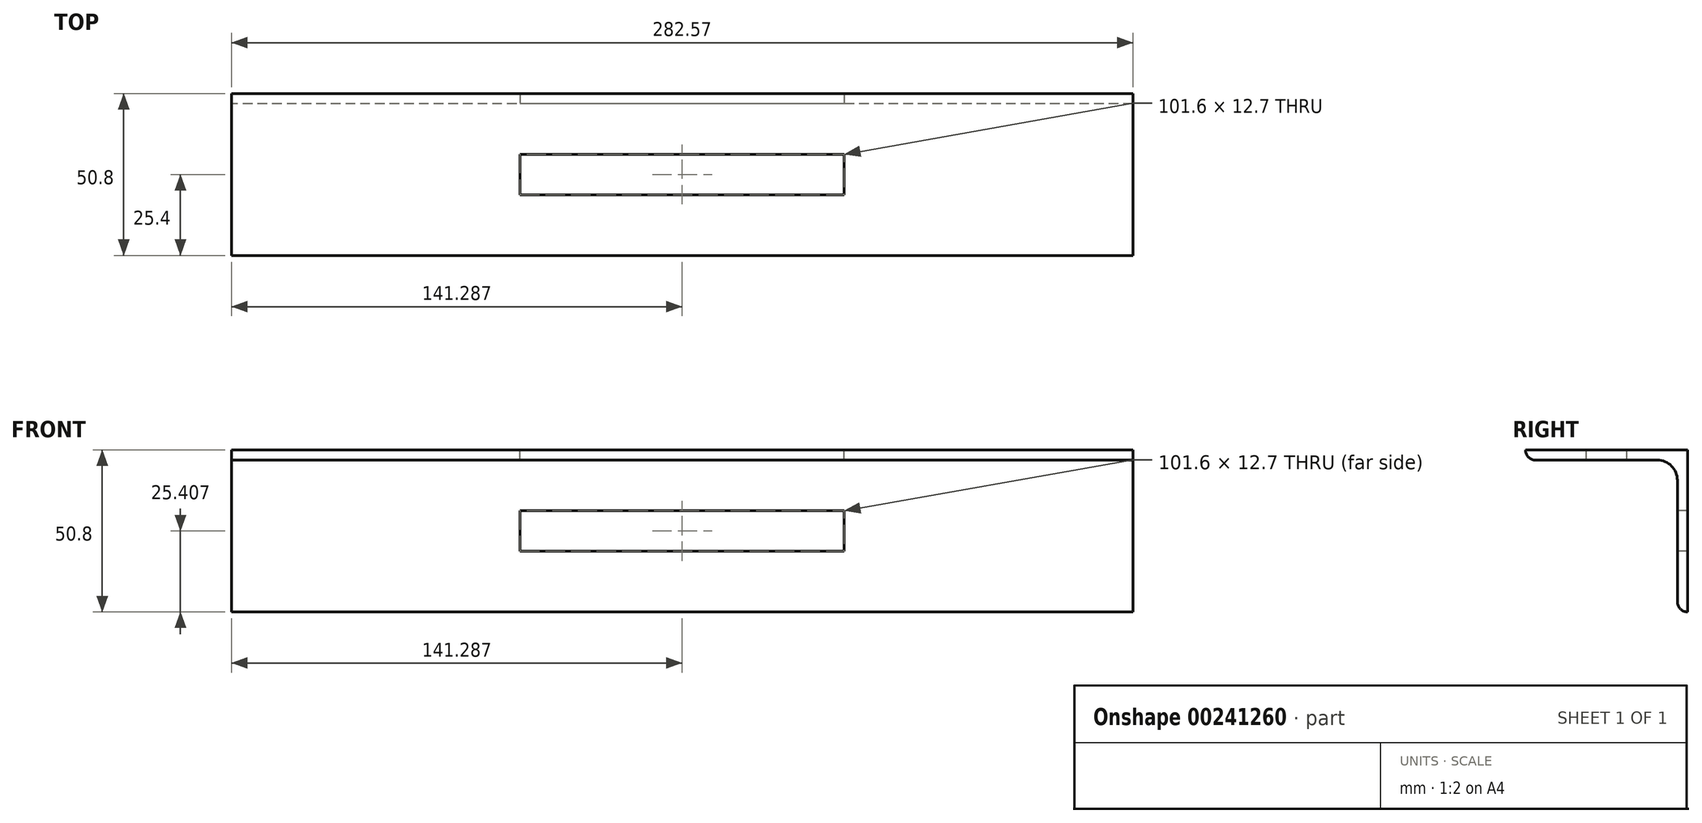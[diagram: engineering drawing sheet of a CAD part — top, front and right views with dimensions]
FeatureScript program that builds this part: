
annotation { "Feature Type Name" : "Feature", "Feature Type Description" : "" }
export const myFeature = defineFeature(function(context is Context, id is Id, definition is map)
    precondition{}
    {
        {
            var Q0;
            Q0=qCreatedBy(makeId("Right.planeOp"),FACE);
            var sketch = newSketch(context, id + "F0", { "sketchPlane" : qUnion([Q0])});
            skLineSegment(sketch, "E0", {"start": v(0, -7.2) * mm, "end": v(0, 43.6) * mm});
            skLineSegment(sketch, "E1", {"start": v(0, 43.6) * mm, "end": v(-50.8, 43.6) * mm});
            skLineSegment(sketch, "E2", {"start": v(-50.8, 43.6) * mm, "end": v(-50.8, 43.6) * mm});
            skLineSegment(sketch, "E3", {"start": v(-47.63, 40.43) * mm, "end": v(-9.52, 40.43) * mm});
            skLineSegment(sketch, "E4", {"start": v(-3.17, 34.08) * mm, "end": v(-3.17, -4.02) * mm});
            skLineSegment(sketch, "E5", {"start": v(-0.1, -7.19) * mm, "end": v(0, -7.2) * mm});
            skPoint(sketch, "E6.visualSharp", {"position": v(-3.17, -7.09) * mm});
            skArc(sketch, "E6.filletArc", {"start": v(-3.17, -4.02) * mm, "mid": v(-2.28, -6.22) * mm, "end": v(-0.1, -7.19) * mm});
            skPoint(sketch, "E7.visualSharp", {"position": v(-50.8, 40.43) * mm});
            skArc(sketch, "E7.filletArc", {"start": v(-50.8, 43.6) * mm, "mid": v(-49.87, 41.36) * mm, "end": v(-47.63, 40.43) * mm});
            skPoint(sketch, "E8.visualSharp", {"position": v(-3.17, 40.43) * mm});
            skArc(sketch, "E8.filletArc", {"start": v(-3.17, 34.08) * mm, "mid": v(-5.03, 38.57) * mm, "end": v(-9.52, 40.43) * mm});
            skSolve(sketch);
        }
        {
            var Q0;
            Q0=makeQuery(id+"F0.imprint","IMPRINT",FACE,{"disambiguationData":[TD([[makeQuery(id+"F0.imprint","IMPRINT",EDGE,{"derivedFrom":sQuery(id+"F0.wireOp",EDGE,"E0")}),1.0]])]});
            extrude(context, id + "F1", {"entities" : qUnion([Q0]), "depth" : 282.57 * mm});
        }
        {
            var Q0;
            Q0=makeQuery(id+"F1.opExtrude","SWEPT_BODY",BODY,{"disambiguationData":[OSD([sQuery(id+"F0.wireOp",EDGE,"E0"),sQuery(id+"F0.wireOp",EDGE,"E1"),sQuery(id+"F0.wireOp",EDGE,"E3"),sQuery(id+"F0.wireOp",EDGE,"E4"),sQuery(id+"F0.wireOp",EDGE,"E5"),sQuery(id+"F0.wireOp",EDGE,"E6.filletArc"),sQuery(id+"F0.wireOp",EDGE,"E7.filletArc"),sQuery(id+"F0.wireOp",EDGE,"E8.filletArc")])]});
            transform(context, id + "F2", {"entities" : qUnion([Q0]), "transformType" : TransformType.TRANSLATION_3D, "dx" : -137.16 * mm, "dy" : 0 * mm, "dz" : 1.52 * mm, "makeCopy" : false});
        }
        {
            var Q0;
            Q0=makeQuery(id+"F1.opExtrude","SWEPT_FACE",FACE,{"disambiguationData":[OSD([sQuery(id+"F0.wireOp",EDGE,"E1")])]});
            var sketch = newSketch(context, id + "F3", { "sketchPlane" : qUnion([Q0])});
            skLineSegment(sketch, "E9.bottom", {"start": v(-137.16, 0) * mm, "end": v(145.42, 0) * mm});
            skLineSegment(sketch, "E9.top", {"start": v(-137.16, -50.8) * mm, "end": v(145.42, -50.8) * mm});
            skLineSegment(sketch, "E9.left", {"start": v(-137.16, 0) * mm, "end": v(-137.16, -50.8) * mm});
            skLineSegment(sketch, "E9.right", {"start": v(145.42, 0) * mm, "end": v(145.42, -50.8) * mm});
            skLineSegment(sketch, "E10.bottom", {"start": v(-46.67, -19.05) * mm, "end": v(54.93, -19.05) * mm});
            skLineSegment(sketch, "E10.top", {"start": v(-46.67, -31.75) * mm, "end": v(54.93, -31.75) * mm});
            skLineSegment(sketch, "E10.left", {"start": v(-46.67, -19.05) * mm, "end": v(-46.67, -31.75) * mm});
            skLineSegment(sketch, "E10.right", {"start": v(54.93, -19.05) * mm, "end": v(54.93, -31.75) * mm});
            skPoint(sketch, "E11", {"position": v(4.13, -50.8) * mm});
            skPoint(sketch, "E12", {"position": v(-46.67, -25.4) * mm});
            skSolve(sketch);
        }
        {
            var Q0;
            Q0=makeQuery(id+"F1.opExtrude","SWEPT_FACE",FACE,{"disambiguationData":[OSD([sQuery(id+"F0.wireOp",EDGE,"E4")])]});
            var sketch = newSketch(context, id + "F4", { "sketchPlane" : qUnion([Q0])});
            skLineSegment(sketch, "E13.bottom", {"start": v(-46.67, 26.09) * mm, "end": v(54.93, 26.09) * mm});
            skLineSegment(sketch, "E13.top", {"start": v(-46.67, 13.39) * mm, "end": v(54.93, 13.39) * mm});
            skLineSegment(sketch, "E13.left", {"start": v(-46.67, 26.09) * mm, "end": v(-46.67, 13.39) * mm});
            skLineSegment(sketch, "E13.right", {"start": v(54.93, 26.09) * mm, "end": v(54.93, 13.39) * mm});
            skPoint(sketch, "E14", {"position": v(-46.67, 19.74) * mm});
            skLineSegment(sketch, "E15.bottom", {"start": v(145.42, -2.5) * mm, "end": v(-137.16, -2.5) * mm});
            skLineSegment(sketch, "E15.top", {"start": v(145.42, 35.6) * mm, "end": v(-137.16, 35.6) * mm});
            skLineSegment(sketch, "E15.left", {"start": v(145.42, -2.5) * mm, "end": v(145.42, 35.6) * mm});
            skLineSegment(sketch, "E15.right", {"start": v(-137.16, -2.5) * mm, "end": v(-137.16, 35.6) * mm});
            skPoint(sketch, "E16", {"position": v(4.13, -2.5) * mm});
            skSolve(sketch);
        }
        {
            var Q0;
            Q0=makeQuery(id+"F4.imprint","IMPRINT",FACE,{"disambiguationData":[TD([[makeQuery(id+"F4.imprint","IMPRINT",EDGE,{"derivedFrom":sQuery(id+"F4.wireOp",EDGE,"E13.bottom")}),-1.0]])]});
            extrude(context, id + "F5", {"entities" : qUnion([Q0]), "operationType" : NewBodyOperationType.REMOVE, "oppositeDirection" : true, "depth" : 25.4 * mm, "hasSecondDirection" : true, "secondDirectionOppositeDirection" : false, "secondDirectionDepth" : 25.4 * mm});
        }
        {
            var Q0;
            Q0=makeQuery(id+"F3.imprint","IMPRINT",FACE,{"disambiguationData":[TD([[makeQuery(id+"F3.imprint","IMPRINT",EDGE,{"derivedFrom":sQuery(id+"F3.wireOp",EDGE,"E10.bottom")}),-1.0]])]});
            extrude(context, id + "F6", {"entities" : qUnion([Q0]), "operationType" : NewBodyOperationType.REMOVE, "oppositeDirection" : true, "depth" : 25.4 * mm, "hasSecondDirection" : true, "secondDirectionOppositeDirection" : false, "secondDirectionDepth" : 25.4 * mm});
        }
    });
